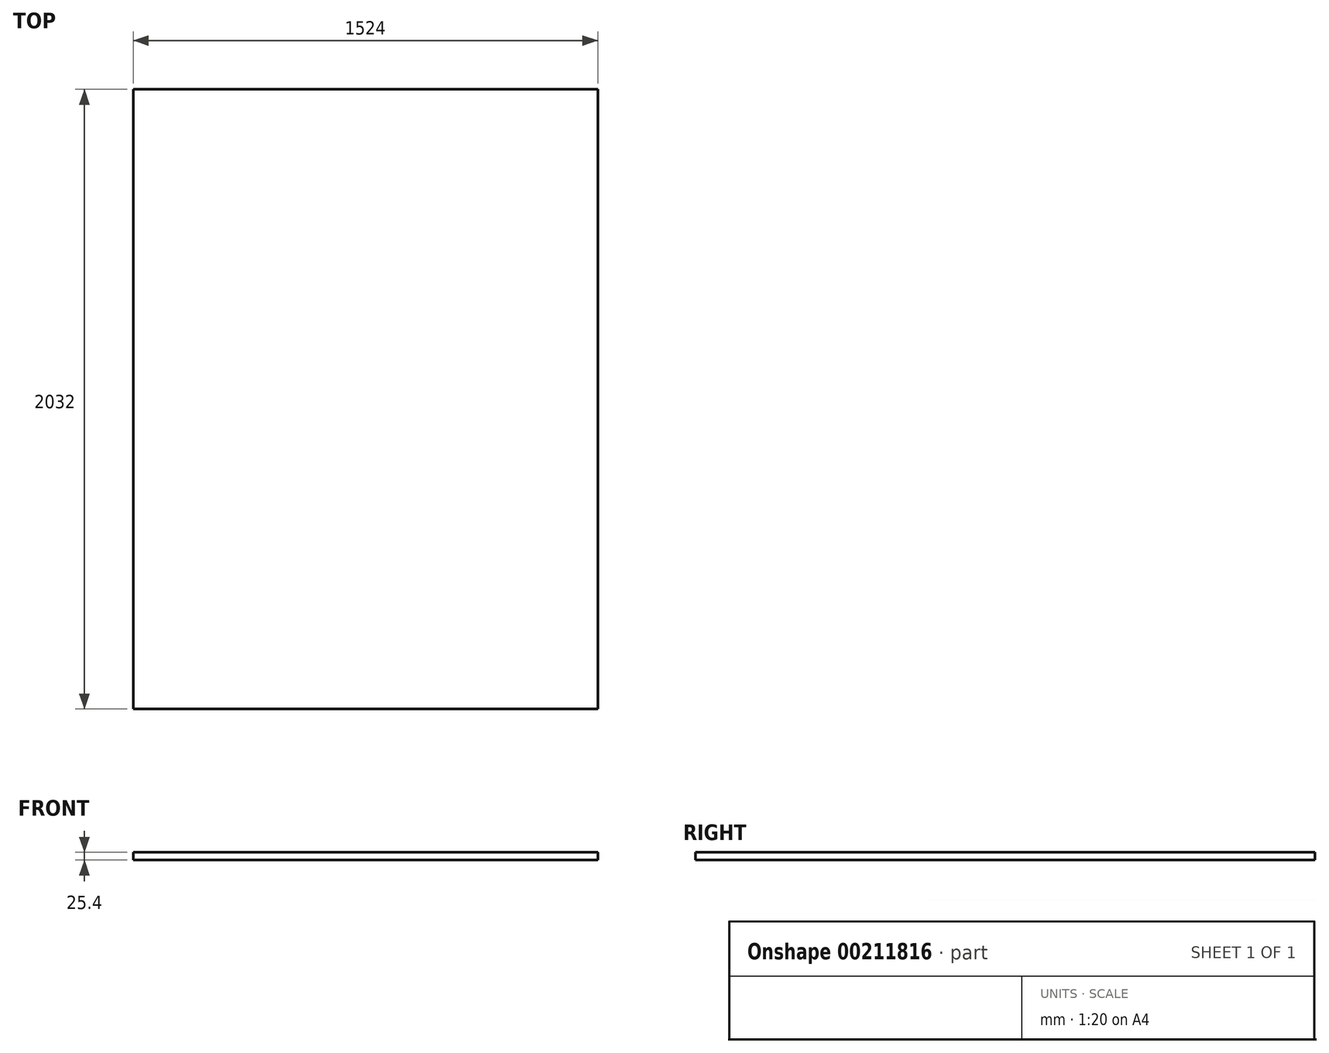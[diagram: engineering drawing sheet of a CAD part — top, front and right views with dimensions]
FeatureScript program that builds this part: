
annotation { "Feature Type Name" : "Feature", "Feature Type Description" : "" }
export const myFeature = defineFeature(function(context is Context, id is Id, definition is map)
    precondition{}
    {
        {
            var Q0;
            Q0=qCreatedBy(makeId("Top.planeOp"),FACE);
            var sketch = newSketch(context, id + "F0", { "sketchPlane" : qUnion([Q0])});
            skLineSegment(sketch, "E0.bottom", {"start": v(0, 0) * mm, "end": v(1524, 0) * mm});
            skLineSegment(sketch, "E0.top", {"start": v(0, 2032) * mm, "end": v(1524, 2032) * mm});
            skLineSegment(sketch, "E0.left", {"start": v(0, 0) * mm, "end": v(0, 2032) * mm});
            skLineSegment(sketch, "E0.right", {"start": v(1524, 0) * mm, "end": v(1524, 2032) * mm});
            skSolve(sketch);
        }
        {
            var Q0;
            Q0=makeQuery(id+"F0.imprint","IMPRINT",FACE,{"disambiguationData":[TD([[makeQuery(id+"F0.imprint","IMPRINT",EDGE,{"derivedFrom":sQuery(id+"F0.wireOp",EDGE,"E0.bottom")}),1.0]])]});
            extrude(context, id + "F1", {"entities" : qUnion([Q0]), "depth" : 25.4 * mm});
        }
    });
